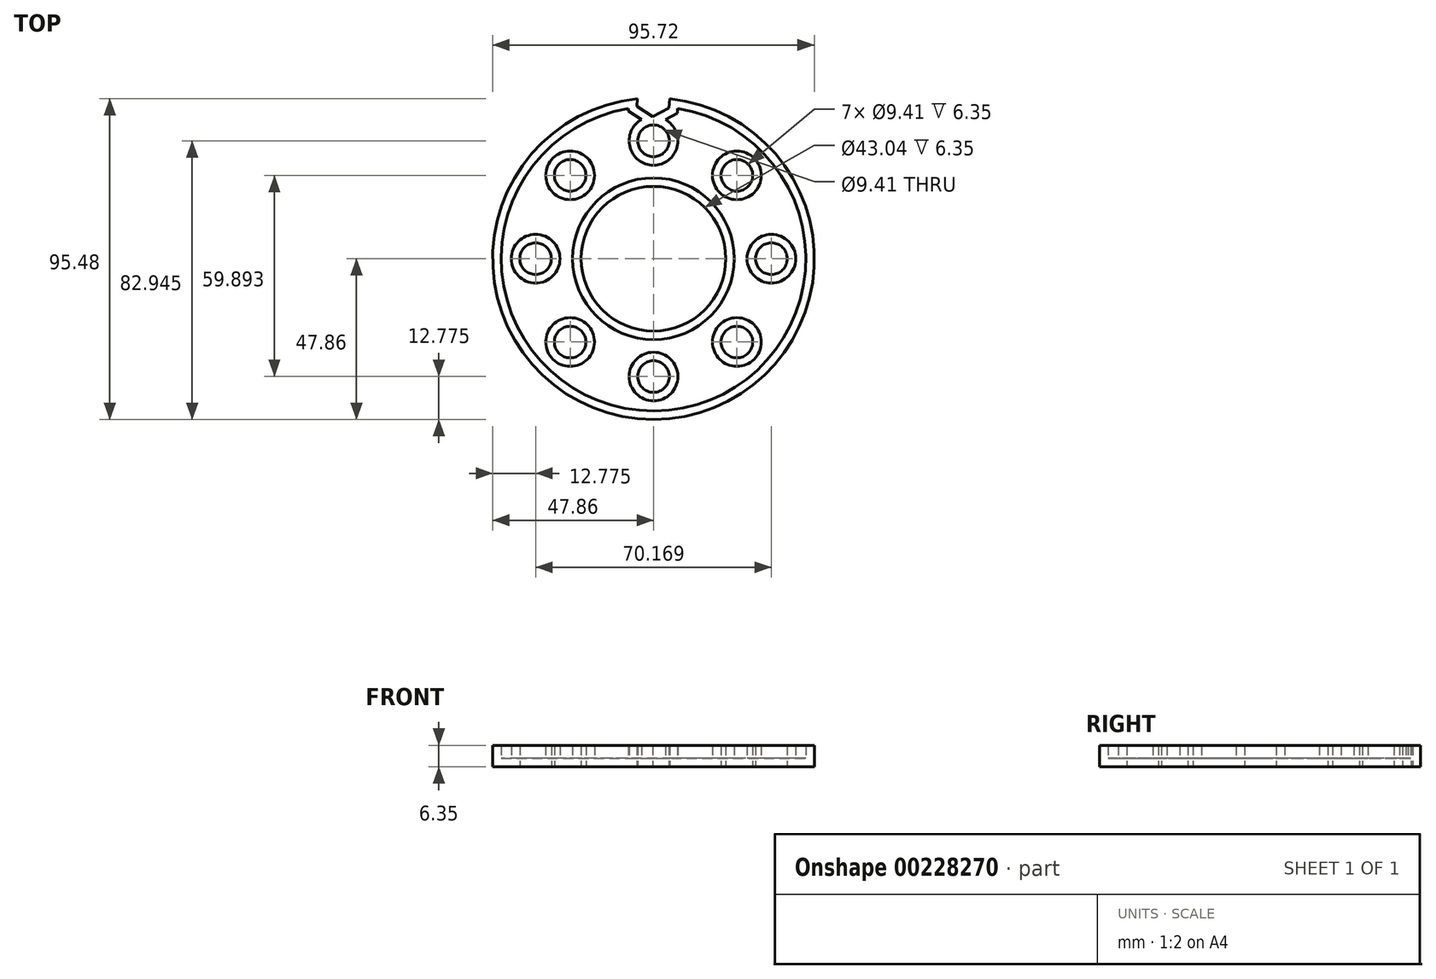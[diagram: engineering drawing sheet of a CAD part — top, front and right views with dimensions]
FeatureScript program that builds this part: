
annotation { "Feature Type Name" : "Feature", "Feature Type Description" : "" }
export const myFeature = defineFeature(function(context is Context, id is Id, definition is map)
    precondition{}
    {
        {
            var Q0;
            Q0=qCreatedBy(makeId("Top.planeOp"),FACE);
            var sketch = newSketch(context, id + "F0", { "sketchPlane" : qUnion([Q0])});
            skLineSegment(sketch, "E0", {"start": v(0, 0) * mm, "end": v(0, 0) * mm});
            skArc(sketch, "E1", {"start": v(-4.78, 47.62) * mm, "mid": v(0, -47.86) * mm, "end": v(4.78, 47.62) * mm});
            skCircle(sketch, "E2", {"center": v(0, 0) * mm, "radius": 21.52 * mm});
            skCircle(sketch, "E3", {"center": v(35.08, 0) * mm, "radius": 4.7 * mm});
            skCircle(sketch, "E4.1.0", {"center": v(24.8, 24.8) * mm, "radius": 4.7 * mm});
            skCircle(sketch, "E4.2.0", {"center": v(0, 35.08) * mm, "radius": 4.7 * mm});
            skCircle(sketch, "E5.1.3.0", {"center": v(-24.8, 24.8) * mm, "radius": 4.7 * mm});
            skCircle(sketch, "E5.1.4.0", {"center": v(-35.08, 0) * mm, "radius": 4.7 * mm});
            skCircle(sketch, "E6.1.5.0", {"center": v(-24.8, -24.8) * mm, "radius": 4.7 * mm});
            skCircle(sketch, "E6.1.6.0", {"center": v(0, -35.08) * mm, "radius": 4.7 * mm});
            skCircle(sketch, "E6.1.7.0", {"center": v(24.8, -24.8) * mm, "radius": 4.7 * mm});
            skArc(sketch, "E7.cCircle", {"start": v(-4.78, 48.1) * mm, "mid": v(-0.24, 43.08) * mm, "end": v(4.78, 47.62) * mm, "construction": true});
            skLineSegment(sketch, "E7.0", {"start": v(4.78, 47.62) * mm, "end": v(4.64, 44.86) * mm});
            skLineSegment(sketch, "E7.1", {"start": v(4.64, 44.86) * mm, "end": v(-0.28, 42.34) * mm});
            skLineSegment(sketch, "E7.2", {"start": v(-0.28, 42.34) * mm, "end": v(-4.92, 45.34) * mm});
            skLineSegment(sketch, "E7.3", {"start": v(-4.92, 45.34) * mm, "end": v(-4.78, 48.1) * mm});
            skPoint(sketch, "E7.0.midPoint", {"position": v(4.78, 47.62) * mm});
            skPoint(sketch, "E8.orphan", {"position": v(4.92, 50.37) * mm});
            skSolve(sketch);
        }
        {
            var Q0;
            Q0=makeQuery(id+"F0.imprint","IMPRINT",FACE,{"disambiguationData":[TD([[makeQuery(id+"F0.imprint","IMPRINT",EDGE,{"derivedFrom":sQuery(id+"F0.wireOp",EDGE,"E2")}),-1.0]])]});
            extrude(context, id + "F1", {"entities" : qUnion([Q0]), "depth" : 6.35 * mm});
        }
        {
            var Q0;
            Q0=makeQuery(id+"F1.opExtrude","CAP_FACE",FACE,{"disambiguationData":[OSD([sQuery(id+"F0.wireOp",EDGE,"E1"),sQuery(id+"F0.wireOp",EDGE,"E2"),sQuery(id+"F0.wireOp",EDGE,"E3"),sQuery(id+"F0.wireOp",EDGE,"E4.1.0"),sQuery(id+"F0.wireOp",EDGE,"E4.2.0"),sQuery(id+"F0.wireOp",EDGE,"E5.1.3.0"),sQuery(id+"F0.wireOp",EDGE,"E5.1.4.0"),sQuery(id+"F0.wireOp",EDGE,"E6.1.5.0"),sQuery(id+"F0.wireOp",EDGE,"E6.1.6.0"),sQuery(id+"F0.wireOp",EDGE,"E6.1.7.0"),sQuery(id+"F0.wireOp",EDGE,"E7.0"),sQuery(id+"F0.wireOp",EDGE,"E7.1"),sQuery(id+"F0.wireOp",EDGE,"E7.2"),sQuery(id+"F0.wireOp",EDGE,"E7.3")])],"isStart":false});
            shell(context, id + "F2", {"entities" : qUnion([Q0]), "thickness" : 2.54 * mm});
        }
    });
